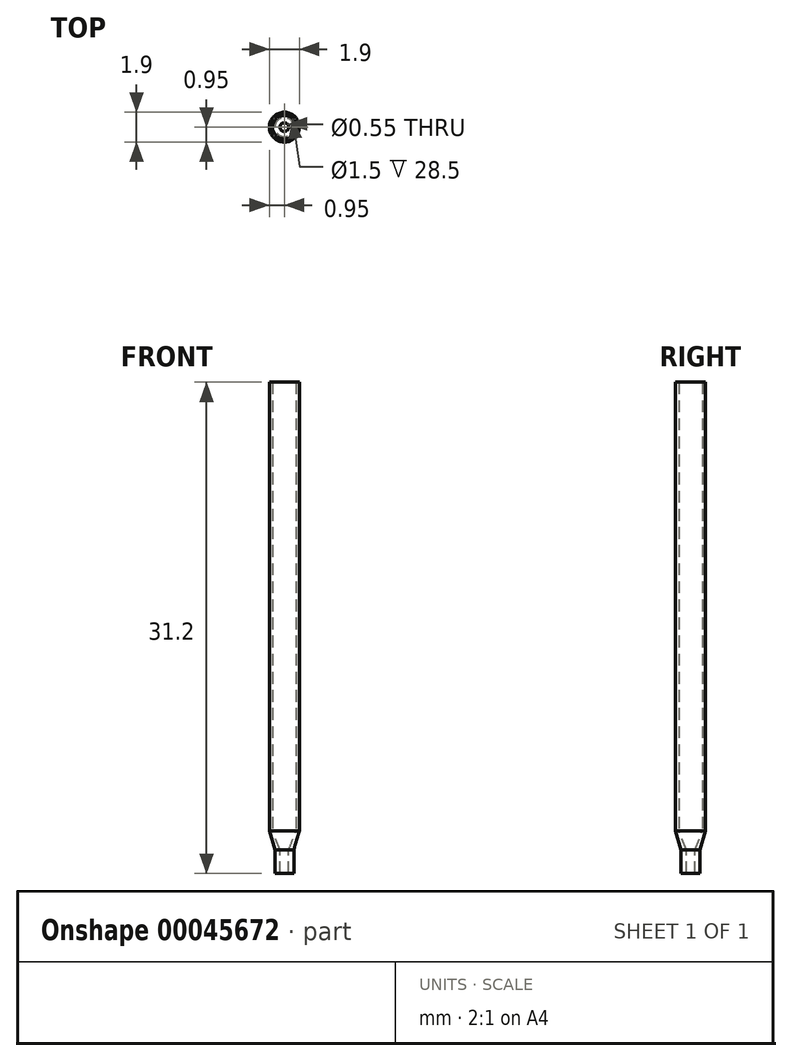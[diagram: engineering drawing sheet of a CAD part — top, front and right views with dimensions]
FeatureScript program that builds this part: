
annotation { "Feature Type Name" : "Feature", "Feature Type Description" : "" }
export const myFeature = defineFeature(function(context is Context, id is Id, definition is map)
    precondition{}
    {
        {
            var Q0;
            Q0=qCreatedBy(makeId("Top.planeOp"),FACE);
            var sketch = newSketch(context, id + "F0", { "sketchPlane" : qUnion([Q0])});
            skCircle(sketch, "E0", {"center": v(0, 0) * mm, "radius": 0.6 * mm});
            skSolve(sketch);
        }
        {
            var Q0;
            Q0=makeQuery(id+"F0.imprint","IMPRINT",FACE,{"disambiguationData":[TD([[makeQuery(id+"F0.imprint","IMPRINT",EDGE,{"derivedFrom":sQuery(id+"F0.wireOp",EDGE,"E0")}),1.0]])]});
            cPlane(context, id + "F1", {"entities" : qUnion([Q0]), "cplaneType" : CPlaneType.OFFSET, "offset" : 1.2 * mm, "width" : 150 * mm, "height" : 150 * mm});
        }
        {
            var Q0;
            Q0=qCreatedBy(id+"F1.planeOp",FACE);
            var sketch = newSketch(context, id + "F2", { "sketchPlane" : qUnion([Q0])});
            skCircle(sketch, "E1", {"center": v(0, 0) * mm, "radius": 0.95 * mm});
            skSolve(sketch);
        }
        {
            var Q0;
            Q0 = qSketchRegion(id + "F0", true);
            var Q1;
            Q1 = qSketchRegion(id + "F2", true);
            loft(context, id + "F3", {"sheetProfilesArray" : [{ "sheetProfileEntities" : qUnion([Q0]) }, { "sheetProfileEntities" : qUnion([Q1]) }]});
        }
        {
            var Q0;
            Q0=makeQuery(id+"F3.opLoft","CAP_FACE",FACE,{"disambiguationData":[OSD([makeQuery(id+"F0.imprint","IMPRINT",FACE,{"disambiguationData":[TD([[makeQuery(id+"F0.imprint","IMPRINT",EDGE,{"derivedFrom":sQuery(id+"F0.wireOp",EDGE,"E0")}),1.0]])]})])],"isStart":true});
            var sketch = newSketch(context, id + "F4", { "sketchPlane" : qUnion([Q0])});
            skCircle(sketch, "E2", {"center": v(0, 0) * mm, "radius": 0.28 * mm});
            skSolve(sketch);
        }
        {
            var Q0;
            Q0=makeQuery(id+"F3.opLoft","CAP_FACE",FACE,{"disambiguationData":[OSD([makeQuery(id+"F2.imprint","IMPRINT",FACE,{"disambiguationData":[TD([[makeQuery(id+"F2.imprint","IMPRINT",EDGE,{"derivedFrom":sQuery(id+"F2.wireOp",EDGE,"E1")}),1.0]])]})])],"isStart":true});
            var sketch = newSketch(context, id + "F5", { "sketchPlane" : qUnion([Q0])});
            skCircle(sketch, "E3", {"center": v(0, 0) * mm, "radius": 0.75 * mm});
            skSolve(sketch);
        }
        {
            var Q1;
            Q1 = qSketchRegion(id + "F5", true);
            var Q2;
            Q2 = qSketchRegion(id + "F4", true);
            loft(context, id + "F6", {"operationType" : NewBodyOperationType.REMOVE, "sheetProfilesArray" : [{ "sheetProfileEntities" : qUnion([Q1]) }, { "sheetProfileEntities" : qUnion([Q2]) }]});
        }
        {
            var Q0;
            Q0=makeQuery(id+"F3.opLoft","CAP_FACE",FACE,{"disambiguationData":[OSD([makeQuery(id+"F0.imprint","IMPRINT",FACE,{"disambiguationData":[TD([[makeQuery(id+"F0.imprint","IMPRINT",EDGE,{"derivedFrom":sQuery(id+"F0.wireOp",EDGE,"E0")}),1.0]])]})])],"isStart":true});
            extrude(context, id + "F7", {"entities" : qUnion([Q0]), "operationType" : NewBodyOperationType.ADD, "depth" : 1.5 * mm});
        }
        {
            var Q0;
            Q0=makeQuery(id+"F3.opLoft","CAP_FACE",FACE,{"disambiguationData":[OSD([makeQuery(id+"F2.imprint","IMPRINT",FACE,{"disambiguationData":[TD([[makeQuery(id+"F2.imprint","IMPRINT",EDGE,{"derivedFrom":sQuery(id+"F2.wireOp",EDGE,"E1")}),1.0]])]})])],"isStart":true});
            extrude(context, id + "F8", {"entities" : qUnion([Q0]), "operationType" : NewBodyOperationType.ADD, "depth" : 28.5 * mm});
        }
    });
